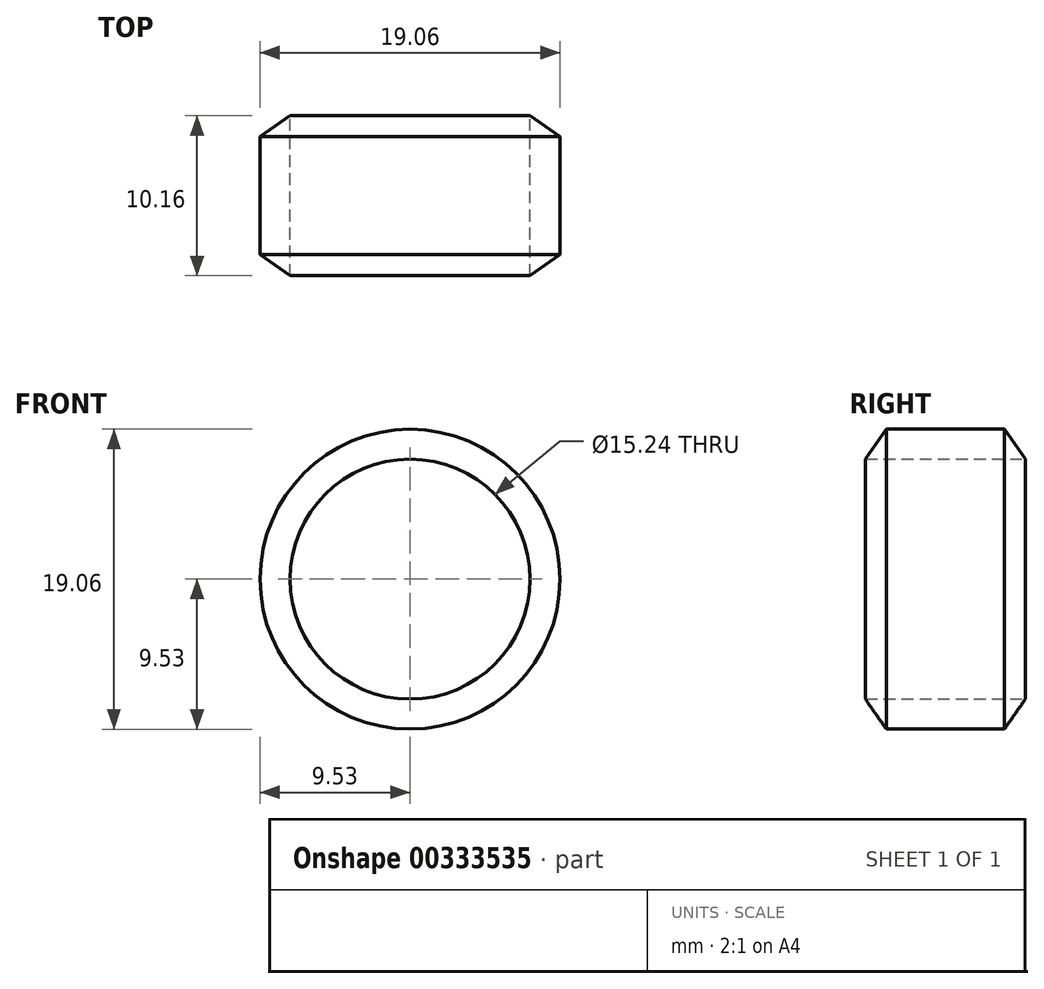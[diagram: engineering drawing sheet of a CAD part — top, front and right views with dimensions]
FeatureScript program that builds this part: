
annotation { "Feature Type Name" : "Feature", "Feature Type Description" : "" }
export const myFeature = defineFeature(function(context is Context, id is Id, definition is map)
    precondition{}
    {
        {
            var Q0;
            Q0=qCreatedBy(makeId("Front.planeOp"),FACE);
            var sketch = newSketch(context, id + "F0", { "sketchPlane" : qUnion([Q0])});
            skCircle(sketch, "E0", {"center": v(0, 0) * mm, "radius": 7.62 * mm});
            skCircle(sketch, "E1", {"center": v(0, 0) * mm, "radius": 9.53 * mm});
            skSolve(sketch);
        }
        {
            var Q0;
            Q0 = qSketchRegion(id + "F0", true);
            extrude(context, id + "F1", {"entities" : qUnion([Q0]), "depth" : 10.16 * mm, "offsetDistance" : 25.4 * mm});
        }
        {
            var Q0;
            Q0=makeQuery(id+"F1.opExtrude","CAP_EDGE",EDGE,{"disambiguationData":[OSD([sQuery(id+"F0.wireOp",EDGE,"E1")])],"isStart":false});
            var Q1;
            Q1=makeQuery(id+"F1.opExtrude","CAP_EDGE",EDGE,{"disambiguationData":[OSD([sQuery(id+"F0.wireOp",EDGE,"E1")])],"isStart":true});
            chamfer(context, id + "F2", {"entities" : qUnion([Q0, Q1]), "chamferType" : ChamferType.OFFSET_ANGLE, "width" : 1.9 * mm, "oppositeDirection" : false, "angle" : 35 * degree, "tangentPropagation" : true});
        }
    });
